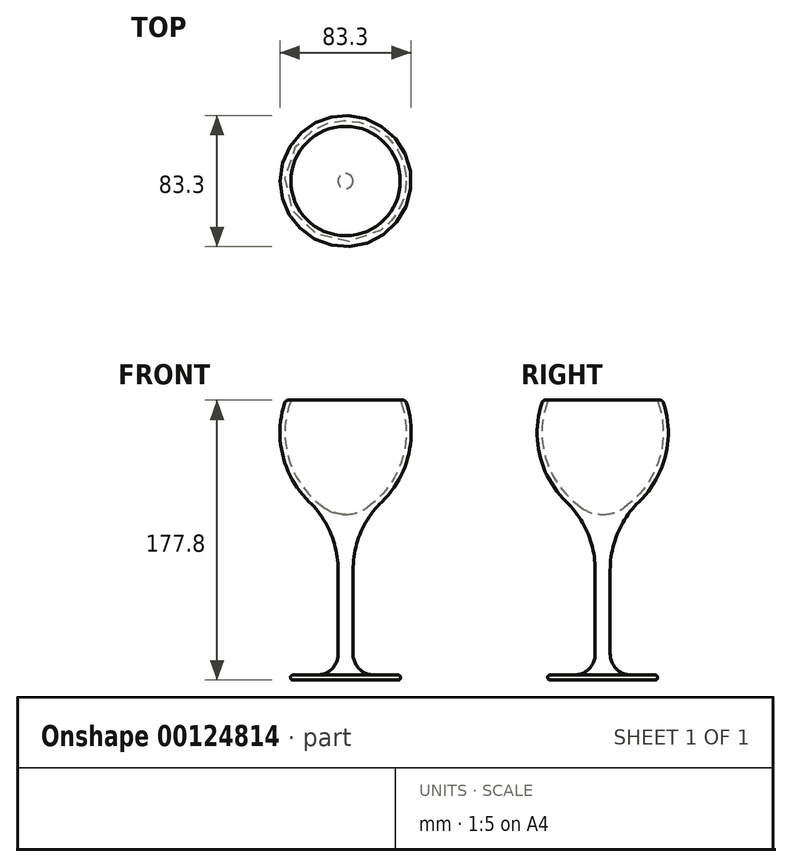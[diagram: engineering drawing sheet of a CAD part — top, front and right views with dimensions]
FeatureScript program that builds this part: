
annotation { "Feature Type Name" : "Feature", "Feature Type Description" : "" }
export const myFeature = defineFeature(function(context is Context, id is Id, definition is map)
    precondition{}
    {
        {
            var Q0;
            Q0=qCreatedBy(makeId("Front.planeOp"),FACE);
            var sketch = newSketch(context, id + "F0", { "sketchPlane" : qUnion([Q0])});
            skLineSegment(sketch, "E0", {"start": v(34.73, 64.58) * mm, "end": v(38.1, 64.58) * mm});
            skLineSegment(sketch, "E1", {"start": v(38.1, 64.58) * mm, "end": v(30.8, 85.12) * mm, "construction": true});
            skArc(sketch, "E2", {"start": v(23.08, 0) * mm, "mid": v(40.06, 30.09) * mm, "end": v(38.1, 64.58) * mm});
            skArc(sketch, "E3", {"start": v(23.08, 0) * mm, "mid": v(9.53, -19.83) * mm, "end": v(4.76, -43.37) * mm});
            skLineSegment(sketch, "E4", {"start": v(4.76, -43.37) * mm, "end": v(4.76, -96.6) * mm});
            skArc(sketch, "E5", {"start": v(4.76, -96.6) * mm, "mid": v(8.7, -106.1) * mm, "end": v(18.22, -110.05) * mm});
            skLineSegment(sketch, "E6", {"start": v(18.22, -110.05) * mm, "end": v(33.4, -110.05) * mm});
            skLineSegment(sketch, "E7", {"start": v(34.93, -111.57) * mm, "end": v(34.93, -111.7) * mm});
            skLineSegment(sketch, "E8", {"start": v(33.4, -113.22) * mm, "end": v(0, -113.22) * mm});
            skLineSegment(sketch, "E9", {"start": v(0, -8.03) * mm, "end": v(0, -113.22) * mm});
            skPoint(sketch, "E10.visualSharp", {"position": v(34.93, -110.05) * mm});
            skArc(sketch, "E10.filletArc", {"start": v(34.93, -111.57) * mm, "mid": v(34.48, -110.5) * mm, "end": v(33.4, -110.05) * mm});
            skPoint(sketch, "E11.visualSharp", {"position": v(34.93, -113.22) * mm});
            skArc(sketch, "E11.filletArc", {"start": v(33.4, -113.22) * mm, "mid": v(34.48, -112.77) * mm, "end": v(34.93, -111.7) * mm});
            skArc(sketch, "E12.0", {"start": v(13.49, -3.8) * mm, "mid": v(35.7, 26.2) * mm, "end": v(35.1, 63.51) * mm});
            skLineSegment(sketch, "E13", {"start": v(35.1, 63.51) * mm, "end": v(32.28, 71.45) * mm, "construction": true});
            skLineSegment(sketch, "E14", {"start": v(35.1, 63.51) * mm, "end": v(34.73, 64.58) * mm});
            skArc(sketch, "E15", {"start": v(0, -8.03) * mm, "mid": v(7.07, -6.95) * mm, "end": v(13.49, -3.8) * mm});
            skPoint(sketch, "E16.orphan", {"position": v(0, 64.58) * mm});
            skSolve(sketch);
        }
        {
            var Q0;
            Q0=makeQuery(id+"F0.imprint","IMPRINT",FACE,{"disambiguationData":[TD([[makeQuery(id+"F0.imprint","IMPRINT",EDGE,{"derivedFrom":sQuery(id+"F0.wireOp",EDGE,"E0")}),-1.0]])]});
            var Q1;
            Q1=sQuery(id+"F0.wireOp",EDGE,"E9");
            revolve(context, id + "F1", {"entities" : qUnion([Q0]), "axis" : qUnion([Q1]), "revolveType" : RevolveType.FULL});
        }
        {
            var Q0;
            Q0=makeQuery(id+"F1.opRevolve","SWEPT_EDGE",EDGE,{"disambiguationData":[OSD([sQuery(id+"F0.wireOp",EDGE,"E12.0"),sQuery(id+"F0.wireOp",EDGE,"E14")])]});
            var Q1;
            Q1=makeQuery(id+"F1.opRevolve","SWEPT_EDGE",EDGE,{"disambiguationData":[OSD([sQuery(id+"F0.wireOp",EDGE,"E0"),sQuery(id+"F0.wireOp",EDGE,"E2")])]});
            fillet(context, id + "F2", {"entities" : qUnion([Q0, Q1]), "radius" : 2.54 * mm, "tangentPropagation" : true, "allowEdgeOverflow" : false});
        }
    });
